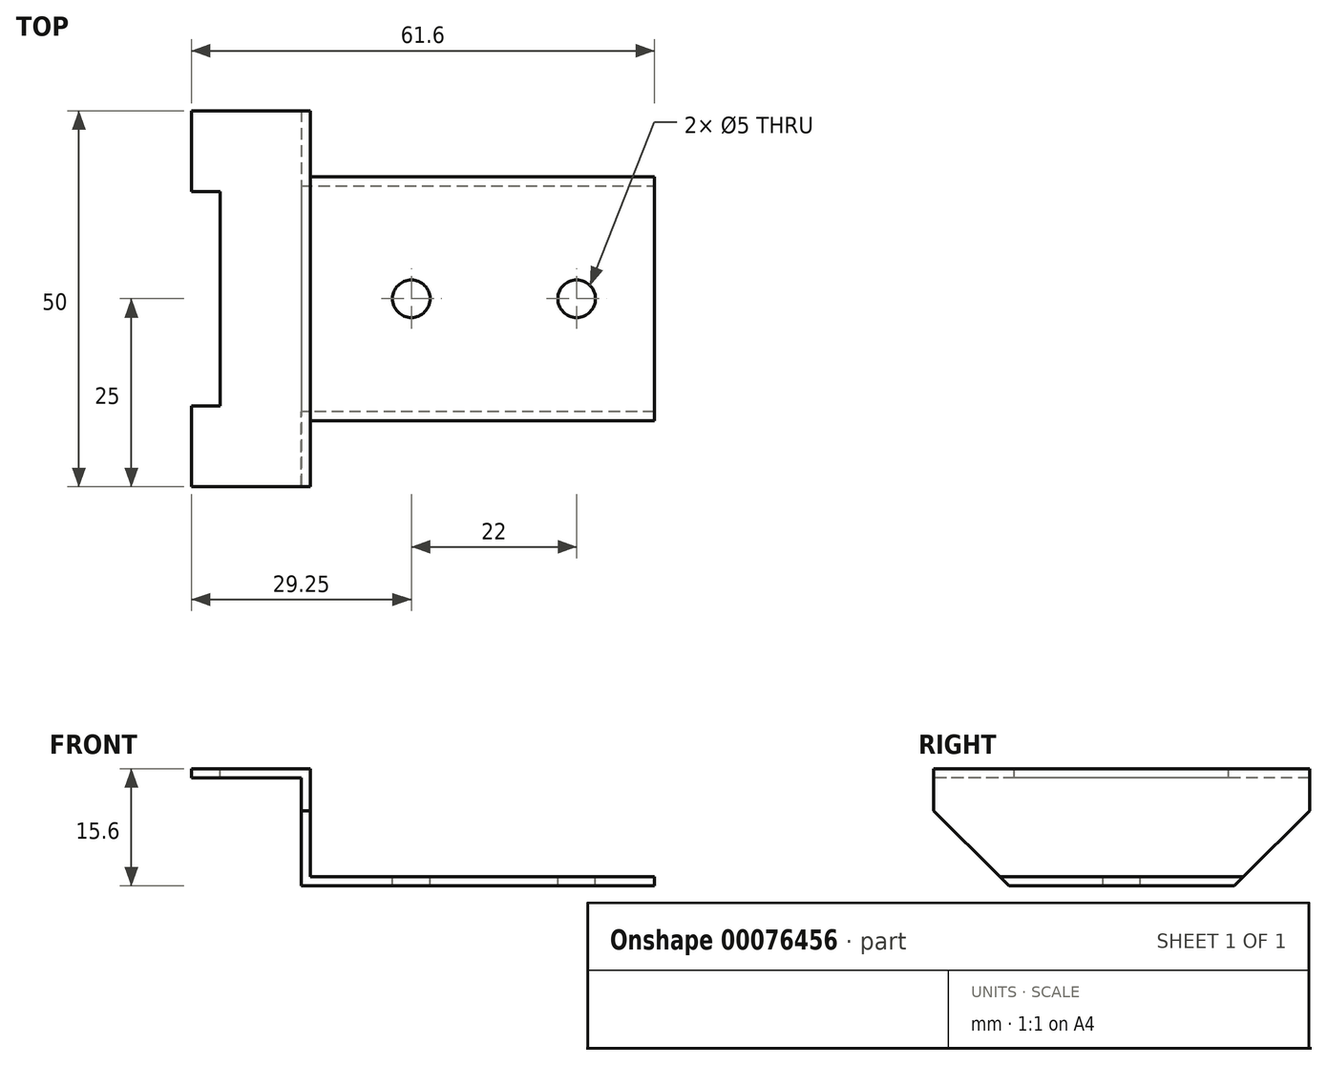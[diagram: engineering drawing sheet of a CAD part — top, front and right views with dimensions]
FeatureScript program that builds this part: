
annotation { "Feature Type Name" : "Feature", "Feature Type Description" : "" }
export const myFeature = defineFeature(function(context is Context, id is Id, definition is map)
    precondition{}
    {
        {
            var Q0;
            Q0=qCreatedBy(makeId("Front.planeOp"),FACE);
            var sketch = newSketch(context, id + "F0", { "sketchPlane" : qUnion([Q0])});
            skLineSegment(sketch, "E0", {"start": v(0, 0) * mm, "end": v(14.6, 0) * mm});
            skLineSegment(sketch, "E1", {"start": v(14.6, 0) * mm, "end": v(14.6, -14.4) * mm});
            skLineSegment(sketch, "E2", {"start": v(14.6, -14.4) * mm, "end": v(61.6, -14.4) * mm});
            skLineSegment(sketch, "E3.0", {"start": v(15.8, -13.2) * mm, "end": v(61.6, -13.2) * mm});
            skLineSegment(sketch, "E3.1", {"start": v(15.8, 1.2) * mm, "end": v(15.8, -13.2) * mm});
            skLineSegment(sketch, "E3.2", {"start": v(0, 1.2) * mm, "end": v(15.8, 1.2) * mm});
            skLineSegment(sketch, "E4", {"start": v(0, 1.2) * mm, "end": v(0, 0) * mm});
            skLineSegment(sketch, "E5", {"start": v(61.6, -13.2) * mm, "end": v(61.6, -14.4) * mm});
            skSolve(sketch);
        }
        {
            var Q0;
            Q0=makeQuery(id+"F0.imprint","IMPRINT",FACE,{"disambiguationData":[TD([[makeQuery(id+"F0.imprint","IMPRINT",EDGE,{"derivedFrom":sQuery(id+"F0.wireOp",EDGE,"E0")}),1.0]])]});
            extrude(context, id + "F1", {"entities" : qUnion([Q0]), "oppositeDirection" : true, "depth" : 50 * mm});
        }
        {
            var Q0;
            Q0=makeQuery(id+"F1.opExtrude","SWEPT_FACE",FACE,{"disambiguationData":[OSD([sQuery(id+"F0.wireOp",EDGE,"E3.2")])]});
            var sketch = newSketch(context, id + "F2", { "sketchPlane" : qUnion([Q0])});
            skLineSegment(sketch, "E6.bottom", {"start": v(-2.2, 10.75) * mm, "end": v(3.8, 10.75) * mm});
            skLineSegment(sketch, "E6.top", {"start": v(-2.2, 39.25) * mm, "end": v(3.8, 39.25) * mm});
            skLineSegment(sketch, "E6.left", {"start": v(-2.2, 10.75) * mm, "end": v(-2.2, 39.25) * mm});
            skLineSegment(sketch, "E6.right", {"start": v(3.8, 10.75) * mm, "end": v(3.8, 39.25) * mm});
            skLineSegment(sketch, "E7", {"start": v(0, 25) * mm, "end": v(15.8, 25) * mm, "construction": true});
            skSolve(sketch);
        }
        {
            var Q0;
            {var subQ0=sQuery(id+"F2.wireOp",EDGE,"E6.right");Q0=makeQuery(id+"F2.imprint","IMPRINT",FACE,{"disambiguationData":[TD([[makeQuery(id+"F2.imprint","IMPRINT",EDGE,{"derivedFrom":subQ0}),1.0]])]});}
            extrude(context, id + "F3", {"entities" : qUnion([Q0]), "operationType" : NewBodyOperationType.REMOVE, "endBound" : BoundingType.THROUGH_ALL, "oppositeDirection" : true, "depth" : 25 * mm});
        }
        {
            var Q0;
            Q0=makeQuery(id+"F1.opExtrude","SWEPT_FACE",FACE,{"disambiguationData":[OSD([sQuery(id+"F0.wireOp",EDGE,"E3.0")])]});
            var sketch = newSketch(context, id + "F4", { "sketchPlane" : qUnion([Q0])});
            skLineSegment(sketch, "E8", {"start": v(61.6, 25) * mm, "end": v(15.8, 25) * mm, "construction": true});
            skPoint(sketch, "E9", {"position": v(51.25, 25) * mm});
            skPoint(sketch, "E10", {"position": v(29.25, 25) * mm});
            skSolve(sketch);
        }
        {
            var Q0;
            Q0=sQuery(id+"F4.wireOp",VERTEX,"E9");
            var Q1;
            Q1=sQuery(id+"F4.wireOp",VERTEX,"E10");
            var Q2;
            Q2=makeQuery(id+"F1.opExtrude","SWEPT_BODY",BODY,{"disambiguationData":[OSD([sQuery(id+"F0.wireOp",EDGE,"E0"),sQuery(id+"F0.wireOp",EDGE,"E1"),sQuery(id+"F0.wireOp",EDGE,"E2"),sQuery(id+"F0.wireOp",EDGE,"E3.0"),sQuery(id+"F0.wireOp",EDGE,"E3.1"),sQuery(id+"F0.wireOp",EDGE,"E3.2"),sQuery(id+"F0.wireOp",EDGE,"E4"),sQuery(id+"F0.wireOp",EDGE,"E5")])]});
            hole(context, id + "F5", {"style" : HoleStyle.SIMPLE, "endStyle" : HoleEndStyle.THROUGH, "standardTappedOrClearance" : lookupTablePath({ "standard" : "ISO", "size" : "5", "type" : "Drilled" }), "standardBlindInLast" : lookupTablePath({ "standard" : "ISO", "size" : "5", "type" : "Drilled" }), "holeDiameter" : 5 * mm, "startFromSketch" : true, "locations" : qUnion([Q0, Q1]), "scope" : qUnion([Q2]), "isTappedThrough" : true});
        }
        {
            var Q0;
            Q0=makeQuery(id+"F1.opExtrude","CAP_EDGE",EDGE,{"disambiguationData":[OSD([sQuery(id+"F0.wireOp",EDGE,"E2")])],"isStart":true});
            var Q1;
            Q1=makeQuery(id+"F1.opExtrude","CAP_EDGE",EDGE,{"disambiguationData":[OSD([sQuery(id+"F0.wireOp",EDGE,"E2")])],"isStart":false});
            chamfer(context, id + "F6", {"entities" : qUnion([Q0, Q1]), "width" : 10 * mm, "tangentPropagation" : true});
        }
    });
